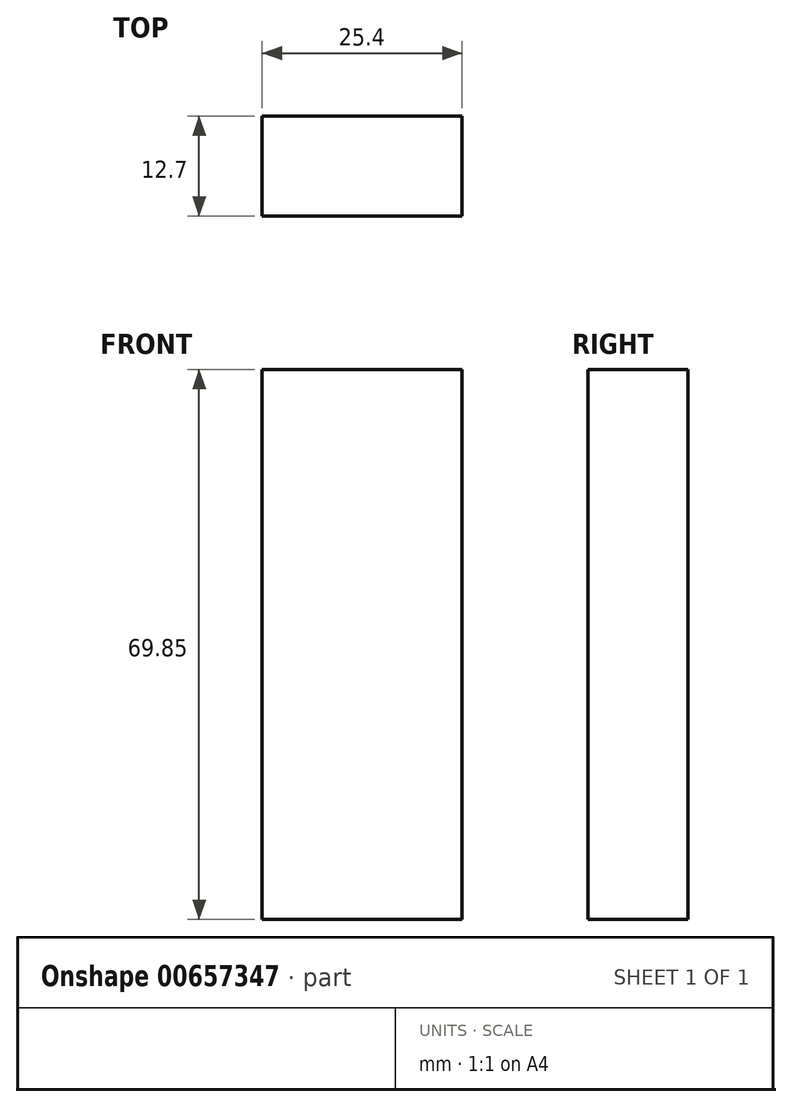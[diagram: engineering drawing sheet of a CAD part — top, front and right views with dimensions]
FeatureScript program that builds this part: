
annotation { "Feature Type Name" : "Feature", "Feature Type Description" : "" }
export const myFeature = defineFeature(function(context is Context, id is Id, definition is map)
    precondition{}
    {
        {
            var Q0;
            Q0=qCreatedBy(makeId("Top.planeOp"),FACE);
            var sketch = newSketch(context, id + "F0", { "sketchPlane" : qUnion([Q0])});
            skLineSegment(sketch, "E0.bottom", {"start": v(0, 0) * mm, "end": v(-76.2, 0) * mm});
            skLineSegment(sketch, "E0.top", {"start": v(0, 50.8) * mm, "end": v(-76.2, 50.8) * mm});
            skLineSegment(sketch, "E0.left", {"start": v(0, 0) * mm, "end": v(0, 50.8) * mm});
            skLineSegment(sketch, "E0.right", {"start": v(-76.2, 0) * mm, "end": v(-76.2, 50.8) * mm});
            skCircle(sketch, "E1", {"center": v(-50.8, 25.4) * mm, "radius": 19.05 * mm});
            skPoint(sketch, "E1.centerSnap0", {"position": v(-76.2, 25.4) * mm});
            skLineSegment(sketch, "E2.bottom", {"start": v(0, 50.8) * mm, "end": v(-25.4, 50.8) * mm});
            skLineSegment(sketch, "E2.top", {"start": v(0, 38.1) * mm, "end": v(-25.4, 38.1) * mm});
            skLineSegment(sketch, "E2.left", {"start": v(0, 50.8) * mm, "end": v(0, 38.1) * mm});
            skLineSegment(sketch, "E2.right", {"start": v(-25.4, 50.8) * mm, "end": v(-25.4, 38.1) * mm});
            skLineSegment(sketch, "E3.bottom", {"start": v(0, 0) * mm, "end": v(-25.4, 0) * mm});
            skLineSegment(sketch, "E3.top", {"start": v(0, 12.7) * mm, "end": v(-25.4, 12.7) * mm});
            skLineSegment(sketch, "E3.left", {"start": v(0, 0) * mm, "end": v(0, 12.7) * mm});
            skLineSegment(sketch, "E3.right", {"start": v(-25.4, 0) * mm, "end": v(-25.4, 12.7) * mm});
            skSolve(sketch);
        }
        {
            var Q0;
            Q0=makeQuery(id+"F0.imprint","IMPRINT",FACE,{"disambiguationData":[TD([[makeQuery(id+"F0.imprint","IMPRINT",EDGE,{"derivedFrom":sQuery(id+"F0.wireOp",EDGE,"E0.bottom")}),-1.0]])]});
            extrude(context, id + "F1", {"entities" : qUnion([Q0]), "depth" : 69.85 * mm, "offsetDistance" : 25.4 * mm});
        }
    });
